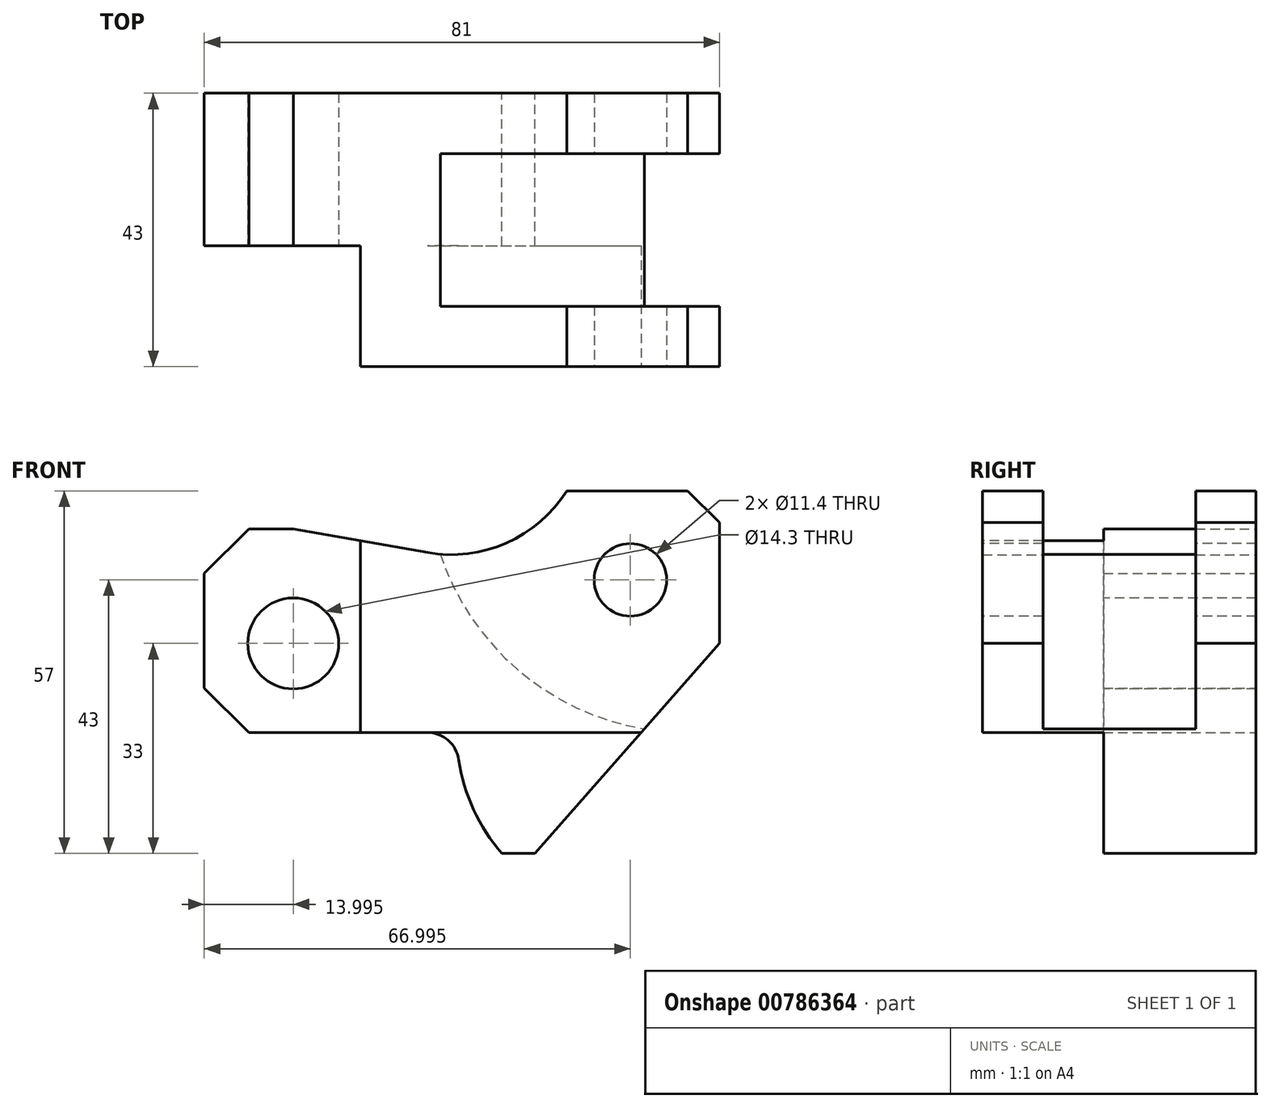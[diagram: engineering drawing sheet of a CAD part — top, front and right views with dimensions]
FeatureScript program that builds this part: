
annotation { "Feature Type Name" : "Feature", "Feature Type Description" : "" }
export const myFeature = defineFeature(function(context is Context, id is Id, definition is map)
    precondition{}
    {
        {
            var Q0;
            Q0=qCreatedBy(makeId("Front.planeOp"),FACE);
            var sketch = newSketch(context, id + "F0", { "sketchPlane" : qUnion([Q0])});
            skLineSegment(sketch, "E0", {"start": v(-44.25, 0) * mm, "end": v(-16.19, 0) * mm});
            skArc(sketch, "E1", {"start": v(-11.24, -4.26) * mm, "mid": v(-12.92, -1.21) * mm, "end": v(-16.19, 0) * mm});
            skArc(sketch, "E2", {"start": v(-11.24, -4.26) * mm, "mid": v(-8.9, -12.12) * mm, "end": v(-4.47, -19) * mm});
            skLineSegment(sketch, "E3", {"start": v(29.75, 14) * mm, "end": v(29.75, 33) * mm});
            skLineSegment(sketch, "E4", {"start": v(29.75, 33) * mm, "end": v(24.75, 38) * mm});
            skLineSegment(sketch, "E5", {"start": v(-4.47, -19) * mm, "end": v(0.75, -19) * mm});
            skLineSegment(sketch, "E6", {"start": v(0.75, -19) * mm, "end": v(29.75, 14) * mm});
            skLineSegment(sketch, "E7", {"start": v(24.75, 38) * mm, "end": v(5.75, 38) * mm});
            skLineSegment(sketch, "E8", {"start": v(-51.25, 7) * mm, "end": v(-51.25, 25) * mm});
            skLineSegment(sketch, "E9", {"start": v(-44.25, 32) * mm, "end": v(-37.25, 32) * mm});
            skLineSegment(sketch, "E10", {"start": v(-51.25, 25) * mm, "end": v(-44.25, 32) * mm});
            skLineSegment(sketch, "E11", {"start": v(-44.25, 0) * mm, "end": v(-51.25, 7) * mm});
            skPoint(sketch, "E12.orphan", {"position": v(-51.25, 32) * mm});
            skPoint(sketch, "E13.orphan", {"position": v(-51.25, 0) * mm});
            skLineSegment(sketch, "E14", {"start": v(-37.25, 32) * mm, "end": v(-16.19, 28.29) * mm});
            skArc(sketch, "E15", {"start": v(-16.19, 28.29) * mm, "mid": v(-3.74, 29.8) * mm, "end": v(5.75, 38) * mm});
            skSolve(sketch);
        }
        {
            var Q0;
            Q0 = qSketchRegion(id + "F0", true);
            extrude(context, id + "F1", {"entities" : qUnion([Q0]), "endBound" : BoundingType.SYMMETRIC, "depth" : 43 * mm, "offsetDistance" : 25.4 * mm});
        }
        {
            var Q0;
            Q0=makeQuery(id+"F1.opExtrude","CAP_FACE",FACE,{"disambiguationData":[OSD([sQuery(id+"F0.wireOp",EDGE,"E0"),sQuery(id+"F0.wireOp",EDGE,"E1"),sQuery(id+"F0.wireOp",EDGE,"E2"),sQuery(id+"F0.wireOp",EDGE,"E3"),sQuery(id+"F0.wireOp",EDGE,"E4"),sQuery(id+"F0.wireOp",EDGE,"E5"),sQuery(id+"F0.wireOp",EDGE,"E6"),sQuery(id+"F0.wireOp",EDGE,"E7"),sQuery(id+"F0.wireOp",EDGE,"E8"),sQuery(id+"F0.wireOp",EDGE,"E9"),sQuery(id+"F0.wireOp",EDGE,"E10"),sQuery(id+"F0.wireOp",EDGE,"E11"),sQuery(id+"F0.wireOp",EDGE,"E14"),sQuery(id+"F0.wireOp",EDGE,"E15")])],"isStart":false});
            var sketch = newSketch(context, id + "F2", { "sketchPlane" : qUnion([Q0])});
            skLineSegment(sketch, "E16", {"start": v(-26.72, 30.14) * mm, "end": v(-26.72, 0) * mm});
            skLineSegment(sketch, "E17", {"start": v(-26.72, 0) * mm, "end": v(17.44, 0) * mm});
            skSolve(sketch);
        }
        {
            var Q0;
            {var subQ1=sQuery(id+"F2.wireOp",EDGE,"E16");Q0=makeQuery(id+"F2.imprint","IMPRINT",FACE,{"disambiguationData":[TD([[makeQuery(id+"F2.imprint","IMPRINT",EDGE,{"derivedFrom":subQ1}),-1.0]])]});}
            var Q1;
            {var subQ4=makeQuery(id+"F1.opExtrude","CAP_EDGE",EDGE,{"disambiguationData":[OSD([sQuery(id+"F0.wireOp",EDGE,"E1")])],"isStart":false});Q1=makeQuery(id+"F2.imprint","IMPRINT",FACE,{"disambiguationData":[TD([[makeQuery(id+"F2.imprint","IMPRINT",EDGE,{"derivedFrom":subQ4}),-1.0]])]});}
            extrude(context, id + "F3", {"entities" : qUnion([Q0, Q1]), "operationType" : NewBodyOperationType.REMOVE, "oppositeDirection" : true, "depth" : 19 * mm, "offsetDistance" : 25.4 * mm});
        }
        {
            var Q0;
            Q0=qCreatedBy(makeId("Front.planeOp"),FACE);
            var sketch = newSketch(context, id + "F4", { "sketchPlane" : qUnion([Q0])});
            skCircle(sketch, "E18", {"center": v(24.75, 41) * mm, "radius": 41 * mm});
            skSolve(sketch);
        }
        {
            var Q0;
            Q0 = qSketchRegion(id + "F4", true);
            extrude(context, id + "F5", {"entities" : qUnion([Q0]), "operationType" : NewBodyOperationType.REMOVE, "endBound" : BoundingType.SYMMETRIC, "oppositeDirection" : true, "depth" : 24 * mm, "offsetDistance" : 25.4 * mm});
        }
        {
            var Q0;
            Q0=makeQuery(id+"F1.opExtrude","CAP_FACE",FACE,{"disambiguationData":[OSD([sQuery(id+"F0.wireOp",EDGE,"E0"),sQuery(id+"F0.wireOp",EDGE,"E1"),sQuery(id+"F0.wireOp",EDGE,"E2"),sQuery(id+"F0.wireOp",EDGE,"E3"),sQuery(id+"F0.wireOp",EDGE,"E4"),sQuery(id+"F0.wireOp",EDGE,"E5"),sQuery(id+"F0.wireOp",EDGE,"E6"),sQuery(id+"F0.wireOp",EDGE,"E7"),sQuery(id+"F0.wireOp",EDGE,"E8"),sQuery(id+"F0.wireOp",EDGE,"E9"),sQuery(id+"F0.wireOp",EDGE,"E10"),sQuery(id+"F0.wireOp",EDGE,"E11"),sQuery(id+"F0.wireOp",EDGE,"E14"),sQuery(id+"F0.wireOp",EDGE,"E15")])],"isStart":false});
            var sketch = newSketch(context, id + "F6", { "sketchPlane" : qUnion([Q0])});
            skCircle(sketch, "E19", {"center": v(15.75, 24) * mm, "radius": 5.7 * mm});
            skSolve(sketch);
        }
        {
            var Q0;
            Q0 = qSketchRegion(id + "F6", true);
            extrude(context, id + "F7", {"entities" : qUnion([Q0]), "operationType" : NewBodyOperationType.REMOVE, "endBound" : BoundingType.THROUGH_ALL, "oppositeDirection" : true, "depth" : 25.4 * mm, "offsetDistance" : 25.4 * mm});
        }
        {
            var Q0;
            Q0=makeQuery(id+"F3.boolean.opBoolean","COPY",FACE,{"derivedFrom":makeQuery(id+"F3.opExtrude","CAP_FACE",FACE,{"disambiguationData":[OSD([sQuery(id+"F0.wireOp",EDGE,"E0"),sQuery(id+"F0.wireOp",EDGE,"E8"),sQuery(id+"F0.wireOp",EDGE,"E9"),sQuery(id+"F0.wireOp",EDGE,"E10"),sQuery(id+"F0.wireOp",EDGE,"E11"),sQuery(id+"F0.wireOp",EDGE,"E14"),sQuery(id+"F2.wireOp",EDGE,"E16")])],"isStart":false})});
            var sketch = newSketch(context, id + "F8", { "sketchPlane" : qUnion([Q0])});
            skCircle(sketch, "E20", {"center": v(-37.25, 14) * mm, "radius": 7.15 * mm});
            skSolve(sketch);
        }
        {
            var Q0;
            Q0 = qSketchRegion(id + "F8", true);
            extrude(context, id + "F9", {"entities" : qUnion([Q0]), "operationType" : NewBodyOperationType.REMOVE, "endBound" : BoundingType.THROUGH_ALL, "oppositeDirection" : true, "depth" : 25.4 * mm, "offsetDistance" : 25.4 * mm});
        }
    });
